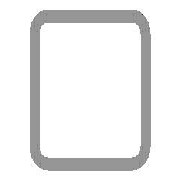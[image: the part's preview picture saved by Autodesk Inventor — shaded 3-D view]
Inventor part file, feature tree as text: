
AUTODESK INVENTOR PART (.ipt)
format: ipt  version: 2022 (Build 260153000, 153)  size: 551,424 bytes
history: native  units: mm (DEFAULTED — no unit token found)
features: other x11, surface_op x4, sketch x2, sweep x1, plane x1
ambient origin geometry x8: Origin, YZ Plane, XZ Plane, XY Plane, X Axis, Y Axis, Z Axis, Center Point
bodies: Body (feature_tree), Solid27 (feature_tree), Solid28 (feature_tree)
feature tree (19):
  parser-record x1  (decoder bookkeeping rows leaked as tree rows — omitted from the tree; the rows remain in map.json)
  other  "Driven Length"
  other  "Start Plane"
  other  "End Plane"
  sweep  "Sweep Path"
  other  "Orientation Work Plane"
  sketch  "Sketch3"  dims[d7=7.5mm d10=40.0mm]
  plane  "Work Plane3"
  sketch  "Sketch4"  dims[d11=40.0mm d12=5.0mm d13=-0.0mm d14=2899.411255mm d15=20.0mm d16=20.0mm d17=90.0deg d18=2899.411255mm d19=0.0mm d20=0.0mm d471=5.0mm d472=5.0mm d473=5.0mm d474=5.0mm d475=5.0mm d476=5.0mm d477=5.0mm d478=5.0mm d479=0.0mm d480=5.0mm d481=5.0mm d482=5.0mm d483=5.0mm d484=5.0mm d485=5.0mm d486=5.0mm d487=5.0mm d488=0.0mm d489=5.0mm d490=5.0mm d491=5.0mm d492=5.0mm d493=5.0mm d494=5.0mm d495=5.0mm d496=5.0mm d497=0.0mm d498=5.0mm d499=5.0mm d500=5.0mm d501=5.0mm d502=5.0mm d503=5.0mm d504=5.0mm d505=5.0mm d506=0.0mm]
  other  "Srf77"
  other  "Srf78"
  other  "Srf80"
  other  "Srf81"
  other  "Srf76"
  surface_op  "Boundary Patch51"
  surface_op  "Boundary Patch52"
  other  "Srf79"
  surface_op  "Boundary Patch53"
  surface_op  "Boundary Patch54"
